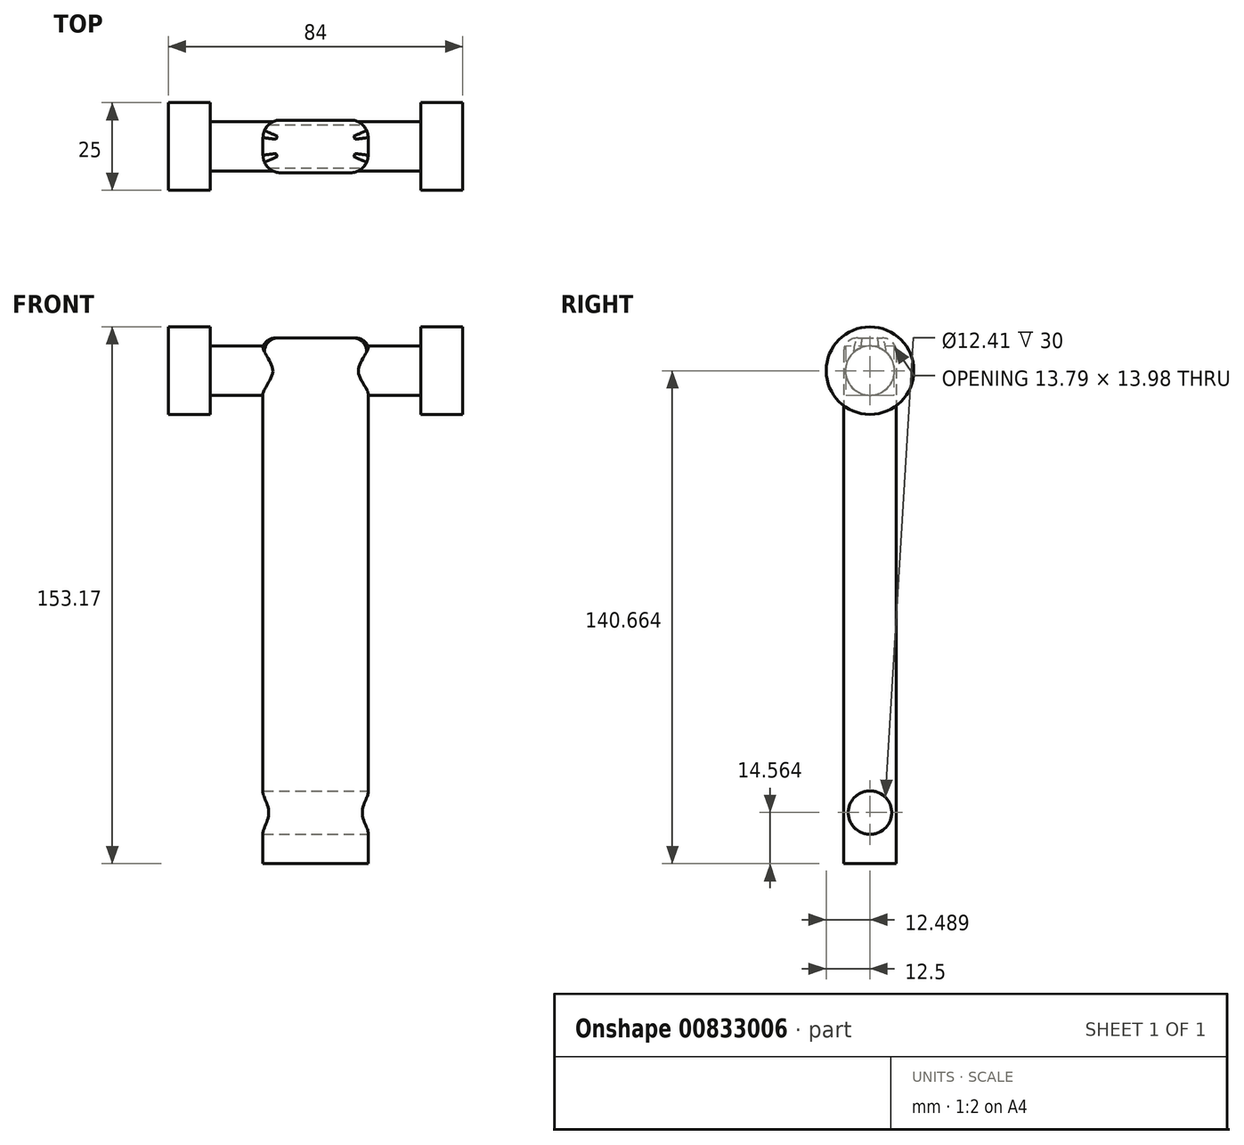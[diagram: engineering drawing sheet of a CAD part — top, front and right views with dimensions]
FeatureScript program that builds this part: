
annotation { "Feature Type Name" : "Feature", "Feature Type Description" : "" }
export const myFeature = defineFeature(function(context is Context, id is Id, definition is map)
    precondition{}
    {
        {
            var Q0;
            Q0=qCreatedBy(makeId("Top.planeOp"),FACE);
            var sketch = newSketch(context, id + "F0", { "sketchPlane" : qUnion([Q0])});
            skLineSegment(sketch, "E0.bottom", {"start": v(-15, 7.5) * mm, "end": v(15, 7.5) * mm});
            skLineSegment(sketch, "E0.top", {"start": v(-15, -7.5) * mm, "end": v(15, -7.5) * mm});
            skLineSegment(sketch, "E0.left", {"start": v(-15, 7.5) * mm, "end": v(-15, -7.5) * mm});
            skLineSegment(sketch, "E0.right", {"start": v(15, 7.5) * mm, "end": v(15, -7.5) * mm});
            skPoint(sketch, "E0.middle", {"position": v(0, 0) * mm});
            skSolve(sketch);
        }
        {
            var Q0;
            Q0 = qSketchRegion(id + "F0", true);
            extrude(context, id + "F1", {"entities" : qUnion([Q0]), "depth" : 150 * mm, "offsetDistance" : 25 * mm});
        }
        {
            var Q0;
            Q0=qCreatedBy(makeId("Right.planeOp"),FACE);
            var sketch = newSketch(context, id + "F2", { "sketchPlane" : qUnion([Q0])});
            skCircle(sketch, "E1", {"center": v(0, 14.56) * mm, "radius": 6.2 * mm});
            skSolve(sketch);
        }
        {
            var Q0;
            Q0 = qSketchRegion(id + "F2", true);
            extrude(context, id + "F3", {"entities" : qUnion([Q0]), "operationType" : NewBodyOperationType.REMOVE, "oppositeDirection" : true, "depth" : 25 * mm, "offsetDistance" : 25 * mm, "hasSecondDirection" : true, "secondDirectionOppositeDirection" : false, "secondDirectionDepth" : 25 * mm});
        }
        {
            var Q0;
            Q0=makeQuery(id+"F1.opExtrude","SWEPT_EDGE",EDGE,{"disambiguationData":[OSD([sQuery(id+"F0.wireOp",EDGE,"E0.top"),sQuery(id+"F0.wireOp",EDGE,"E0.right")])]});
            var Q1;
            Q1=makeQuery(id+"F1.opExtrude","SWEPT_EDGE",EDGE,{"disambiguationData":[OSD([sQuery(id+"F0.wireOp",EDGE,"E0.bottom"),sQuery(id+"F0.wireOp",EDGE,"E0.right")])]});
            var Q2;
            Q2=makeQuery(id+"F1.opExtrude","SWEPT_EDGE",EDGE,{"disambiguationData":[OSD([sQuery(id+"F0.wireOp",EDGE,"E0.top"),sQuery(id+"F0.wireOp",EDGE,"E0.left")])]});
            var Q3;
            Q3=makeQuery(id+"F1.opExtrude","SWEPT_EDGE",EDGE,{"disambiguationData":[OSD([sQuery(id+"F0.wireOp",EDGE,"E0.bottom"),sQuery(id+"F0.wireOp",EDGE,"E0.left")])]});
            fillet(context, id + "F4", {"entities" : qUnion([Q0, Q1, Q2, Q3]), "radius" : 5 * mm, "tangentPropagation" : true, "allowEdgeOverflow" : false});
        }
        {
            var Q0;
            Q0=qCreatedBy(makeId("Right.planeOp"),FACE);
            var sketch = newSketch(context, id + "F5", { "sketchPlane" : qUnion([Q0])});
            skCircle(sketch, "E2", {"center": v(0, 140.67) * mm, "radius": 7 * mm});
            skSolve(sketch);
        }
        {
            var Q0;
            Q0 = qSketchRegion(id + "F5", true);
            var Q1;
            Q1 = qSketchRegion(id + "F7", true);
            extrude(context, id + "F6", {"entities" : qUnion([Q0, Q1]), "operationType" : NewBodyOperationType.ADD, "depth" : 30 * mm, "offsetDistance" : 25 * mm, "hasSecondDirection" : true, "secondDirectionOppositeDirection" : true, "secondDirectionDepth" : 30 * mm});
        }
        {
            var Q0;
            Q0=makeQuery(id+"F6.opExtrude","CAP_FACE",FACE,{"disambiguationData":[OSD([sQuery(id+"F5.wireOp",EDGE,"E2")])],"isStart":true});
            var sketch = newSketch(context, id + "F7", { "sketchPlane" : qUnion([Q0])});
            skCircle(sketch, "E3", {"center": v(0, 140.67) * mm, "radius": 12.5 * mm});
            skSolve(sketch);
        }
        {
            var Q0;
            Q0 = qSketchRegion(id + "F7", true);
            extrude(context, id + "F8", {"entities" : qUnion([Q0]), "operationType" : NewBodyOperationType.ADD, "depth" : 12 * mm, "offsetDistance" : 25 * mm});
        }
        {
            var Q0;
            Q0=makeQuery(id+"F6.opExtrude","CAP_FACE",FACE,{"disambiguationData":[OSD([sQuery(id+"F5.wireOp",EDGE,"E2")])],"isStart":false});
            var sketch = newSketch(context, id + "F9", { "sketchPlane" : qUnion([Q0])});
            skCircle(sketch, "E4", {"center": v(0, 140.67) * mm, "radius": 12.5 * mm});
            skSolve(sketch);
        }
        {
            var Q0;
            Q0 = qSketchRegion(id + "F9", true);
            extrude(context, id + "F10", {"entities" : qUnion([Q0]), "operationType" : NewBodyOperationType.ADD, "depth" : 12 * mm, "offsetDistance" : 25 * mm});
        }
        {
            var Q0;
            Q0=makeQuery(id+"F1.opExtrude","CAP_FACE",FACE,{"disambiguationData":[OSD([sQuery(id+"F0.wireOp",EDGE,"E0.bottom"),sQuery(id+"F0.wireOp",EDGE,"E0.top"),sQuery(id+"F0.wireOp",EDGE,"E0.left"),sQuery(id+"F0.wireOp",EDGE,"E0.right")])],"isStart":false});
            fillet(context, id + "F11", {"entities" : qUnion([Q0]), "radius" : 4 * mm, "tangentPropagation" : true, "allowEdgeOverflow" : false});
        }
    });
